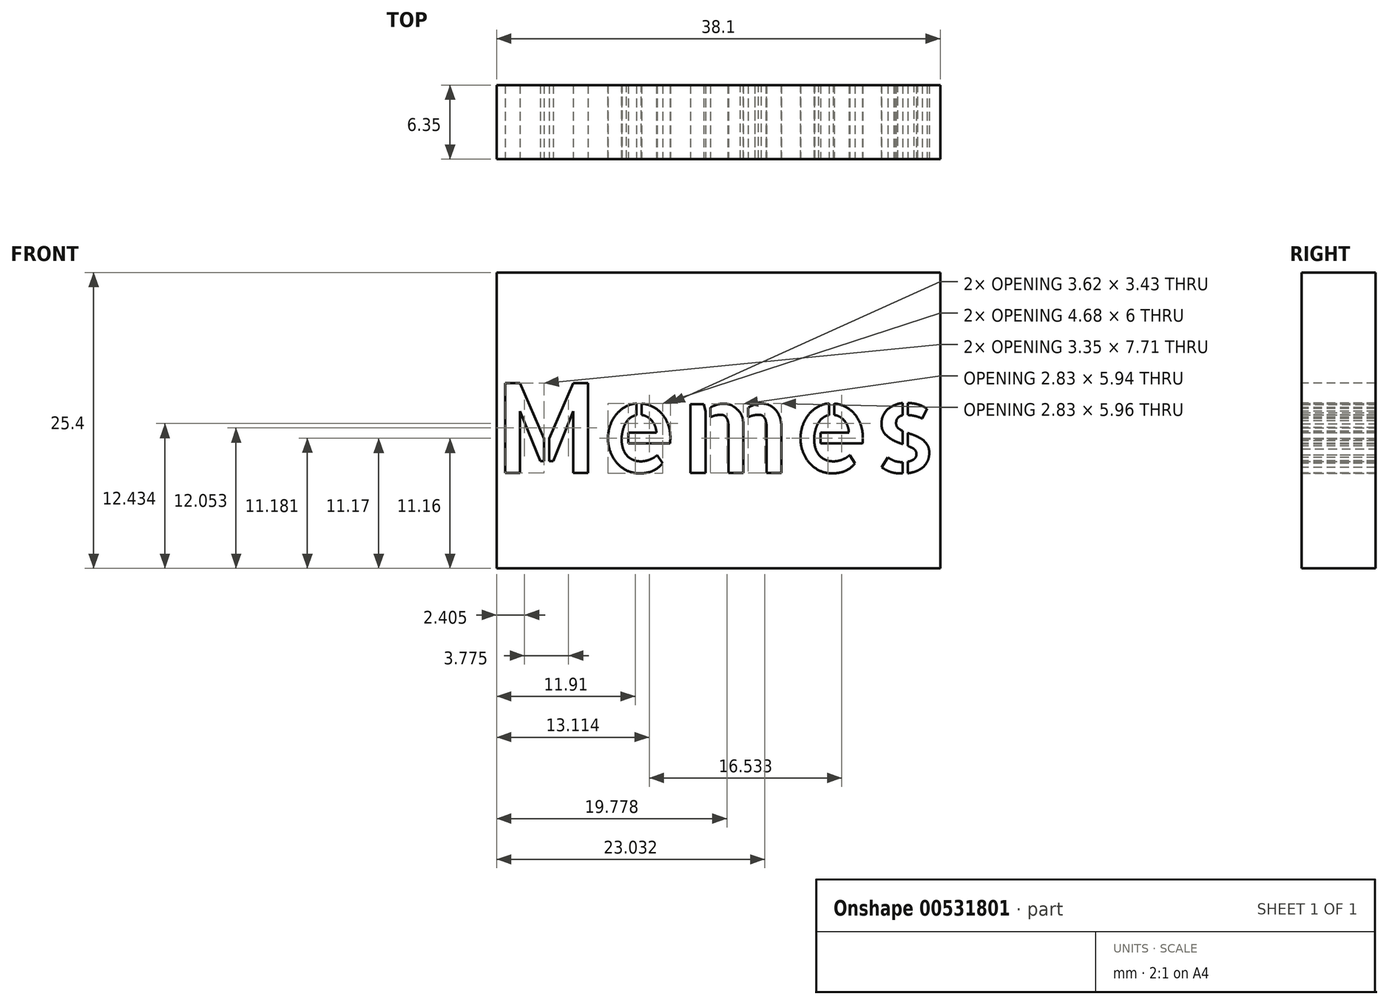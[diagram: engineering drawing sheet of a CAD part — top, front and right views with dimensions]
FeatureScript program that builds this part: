
annotation { "Feature Type Name" : "Feature", "Feature Type Description" : "" }
export const myFeature = defineFeature(function(context is Context, id is Id, definition is map)
    precondition{}
    {
        {
            var Q0;
            Q0=qCreatedBy(makeId("Front.planeOp"),FACE);
            var sketch = newSketch(context, id + "F0", { "sketchPlane" : qUnion([Q0])});
            skLineSegment(sketch, "E0.bottom", {"start": v(-52.04, 45.17) * mm, "end": v(-13.94, 45.17) * mm});
            skLineSegment(sketch, "E0.top", {"start": v(-52.04, 19.77) * mm, "end": v(-13.94, 19.77) * mm});
            skLineSegment(sketch, "E0.left", {"start": v(-52.04, 45.17) * mm, "end": v(-52.04, 19.77) * mm});
            skLineSegment(sketch, "E0.right", {"start": v(-13.94, 45.17) * mm, "end": v(-13.94, 19.77) * mm});
            skSolve(sketch);
        }
        {
            var Q0;
            Q0 = qSketchRegion(id + "F0", true);
            extrude(context, id + "F1", {"entities" : qUnion([Q0]), "depth" : 6.35 * mm, "offsetDistance" : 25.4 * mm});
        }
        {
            var Q0;
            Q0=makeQuery(id+"F1.opExtrude","CAP_FACE",FACE,{"disambiguationData":[OSD([sQuery(id+"F0.wireOp",EDGE,"E0.bottom"),sQuery(id+"F0.wireOp",EDGE,"E0.top"),sQuery(id+"F0.wireOp",EDGE,"E0.left"),sQuery(id+"F0.wireOp",EDGE,"E0.right")])],"isStart":false});
            var sketch = newSketch(context, id + "F2", { "sketchPlane" : qUnion([Q0])});
            skText(sketch, "E1", { "text": "Memes", "fontName": "AllertaStencil-Regular.ttf"});
            const initialGuessF2  = {"E1": [-0.05227, 0.02797, 1, 0, 0.00771]};
            skSetInitialGuess(sketch, initialGuessF2);
            skSolve(sketch);
        }
        {
            var Q0;
            Q0 = qSketchRegion(id + "F2", true);
            extrude(context, id + "F3", {"entities" : qUnion([Q0]), "operationType" : NewBodyOperationType.REMOVE, "oppositeDirection" : true, "depth" : 25.9 * mm, "offsetDistance" : 25.4 * mm});
        }
    });
